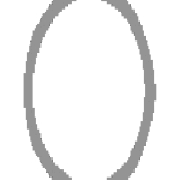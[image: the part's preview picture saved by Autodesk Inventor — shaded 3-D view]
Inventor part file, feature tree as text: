
AUTODESK INVENTOR PART (.ipt)
format: ipt  version: 2021 (Build 250183000, 183)  size: 112,128 bytes
history: native  units: in
note: dims shown in document units (in); Inventor stores cm internally (conversion verified against a paired STEP export)
features: other x4, sketch x3, plane x1
ambient origin geometry x8: Origin, YZ Plane, XZ Plane, XY Plane, X Axis, Y Axis, Z Axis, Center Point
bodies: Solid1 (feature_tree), Body (feature_tree)
feature tree (8):
  other  "Driven Length"
  other  "Frame Generator"
  other  "Start Plane"
  other  "End Plane"
  sketch  "Sketch"  dims[d2=6.0828in d4=-0.0in d5=6.0828in d6=0.12in d7=0.0in d8=90.0deg d9=6.0828in]
  sketch  "Sketch2"  dims[d0=1.0in]
  plane  "Work Plane3"
  sketch  "Sketch3"  dims[d1=0.065in]
